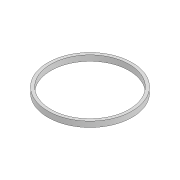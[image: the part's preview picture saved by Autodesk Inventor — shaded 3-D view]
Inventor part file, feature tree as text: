
AUTODESK INVENTOR PART (.ipt)
format: ipt  version: 2022 (Build 260153000, 153)  size: 86,016 bytes
history: native  units: mm
features: extrude x1, sketch x1
ambient origin geometry x8: Origin, YZ Plane, XZ Plane, XY Plane, X Axis, Y Axis, Z Axis, Center Point
bodies: Solid1 (feature_tree)
feature tree (2):
  extrude  "Extrusion1"  Depth=2.83mm
  sketch  "Sketch1"  dims[d0=40.0mm d1=1.5mm d2=2.83mm d3=0.0mm]
